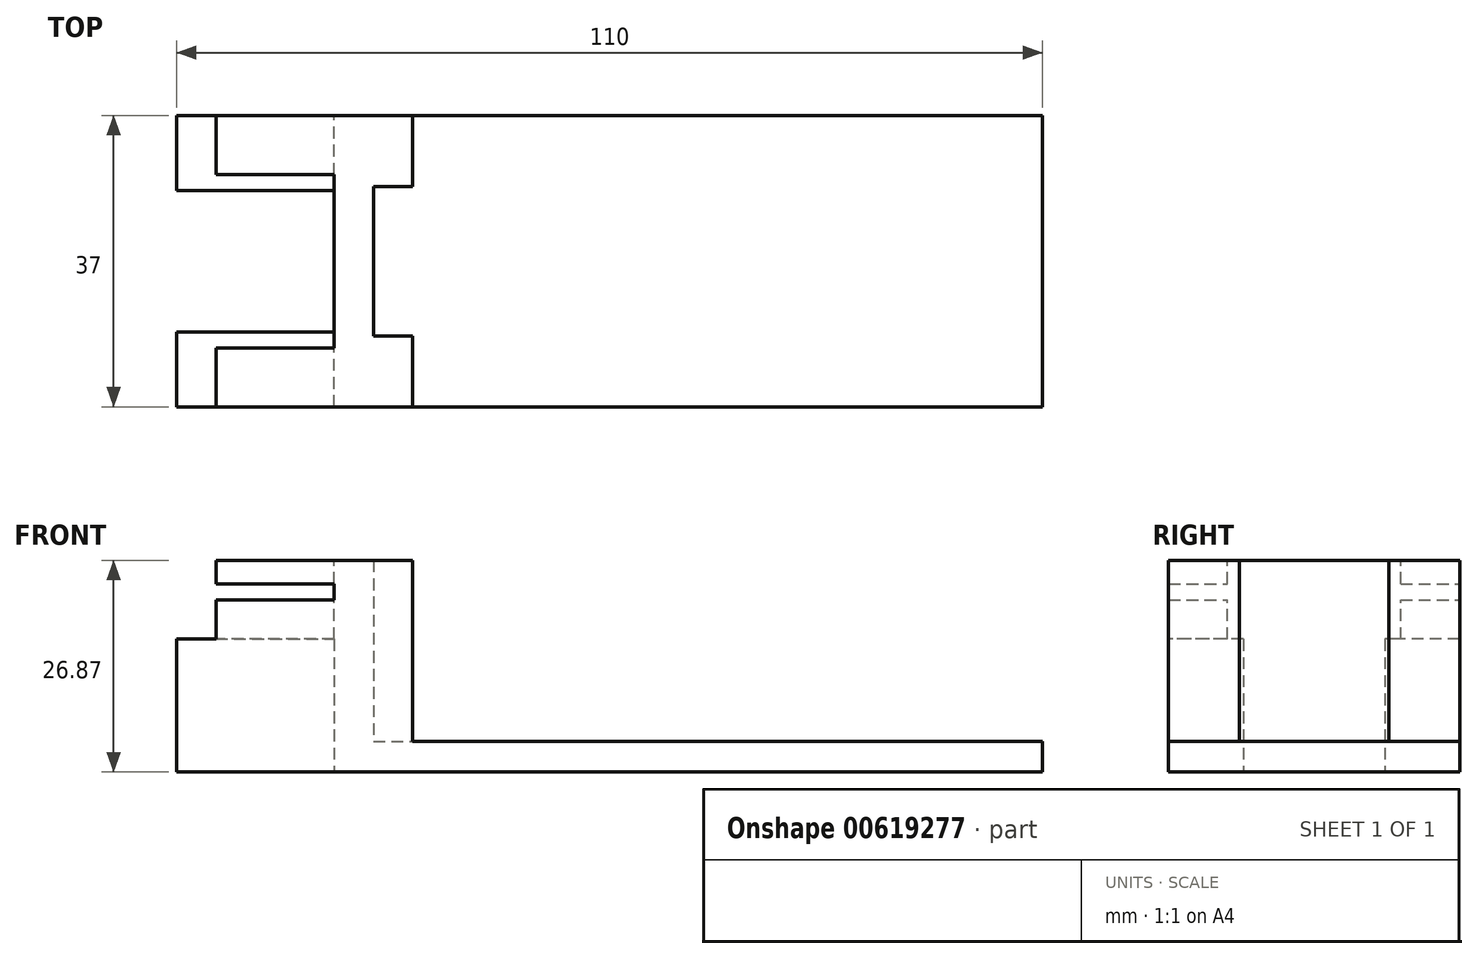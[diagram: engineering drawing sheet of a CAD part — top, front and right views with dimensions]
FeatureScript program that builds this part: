
annotation { "Feature Type Name" : "Feature", "Feature Type Description" : "" }
export const myFeature = defineFeature(function(context is Context, id is Id, definition is map)
    precondition{}
    {
        {
            var Q0;
            Q0=qCreatedBy(makeId("Front.planeOp"),FACE);
            var sketch = newSketch(context, id + "F0", { "sketchPlane" : qUnion([Q0])});
            skLineSegment(sketch, "E0.bottom", {"start": v(-14.48, -27.76) * mm, "end": v(15.52, -27.76) * mm});
            skLineSegment(sketch, "E0.top", {"start": v(-14.48, -54.63) * mm, "end": v(15.52, -54.63) * mm});
            skLineSegment(sketch, "E0.left", {"start": v(-14.48, -27.76) * mm, "end": v(-14.48, -54.63) * mm});
            skLineSegment(sketch, "E0.right", {"start": v(15.52, -27.76) * mm, "end": v(15.52, -50.78) * mm});
            skLineSegment(sketch, "E1.bottom", {"start": v(15.52, -54.63) * mm, "end": v(95.52, -54.63) * mm});
            skLineSegment(sketch, "E1.top", {"start": v(15.52, -50.78) * mm, "end": v(95.52, -50.78) * mm});
            skLineSegment(sketch, "E1.right", {"start": v(95.52, -54.63) * mm, "end": v(95.52, -50.78) * mm});
            skSolve(sketch);
        }
        {
            var Q0;
            Q0 = qSketchRegion(id + "F0", true);
            extrude(context, id + "F1", {"entities" : qUnion([Q0]), "depth" : 37 * mm, "offsetDistance" : 25.4 * mm});
        }
        {
            var Q0;
            Q0=makeQuery(id+"F1.opExtrude","SWEPT_FACE",FACE,{"disambiguationData":[OSD([sQuery(id+"F0.wireOp",EDGE,"E0.right")])]});
            var sketch = newSketch(context, id + "F2", { "sketchPlane" : qUnion([Q0])});
            skLineSegment(sketch, "E2.bottom", {"start": v(-28, -27.76) * mm, "end": v(-9, -27.76) * mm});
            skLineSegment(sketch, "E2.top", {"start": v(-28, -50.78) * mm, "end": v(-9, -50.78) * mm});
            skLineSegment(sketch, "E2.left", {"start": v(-28, -27.76) * mm, "end": v(-28, -50.78) * mm});
            skLineSegment(sketch, "E2.right", {"start": v(-9, -27.76) * mm, "end": v(-9, -50.78) * mm});
            skSolve(sketch);
        }
        {
            var Q0;
            Q0 = qSketchRegion(id + "F2", true);
            extrude(context, id + "F3", {"entities" : qUnion([Q0]), "operationType" : NewBodyOperationType.REMOVE, "oppositeDirection" : true, "depth" : 5 * mm, "offsetDistance" : 25.4 * mm});
        }
        {
            var Q0;
            Q0=makeQuery(id+"F1.opExtrude","SWEPT_FACE",FACE,{"disambiguationData":[OSD([sQuery(id+"F0.wireOp",EDGE,"E0.left")])]});
            var sketch = newSketch(context, id + "F4", { "sketchPlane" : qUnion([Q0])});
            skLineSegment(sketch, "E3.bottom", {"start": v(27.5, -27.76) * mm, "end": v(9.5, -27.76) * mm});
            skLineSegment(sketch, "E3.top", {"start": v(27.5, -54.63) * mm, "end": v(9.5, -54.63) * mm});
            skLineSegment(sketch, "E3.left", {"start": v(27.5, -27.76) * mm, "end": v(27.5, -54.63) * mm});
            skLineSegment(sketch, "E3.right", {"start": v(9.5, -27.76) * mm, "end": v(9.5, -54.63) * mm});
            skSolve(sketch);
        }
        {
            var Q0;
            Q0 = qSketchRegion(id + "F4", true);
            extrude(context, id + "F5", {"entities" : qUnion([Q0]), "operationType" : NewBodyOperationType.REMOVE, "oppositeDirection" : true, "depth" : 20 * mm, "offsetDistance" : 25.4 * mm});
        }
        {
            var Q0;
            {var subQ2=sQuery(id+"F0.wireOp",EDGE,"E0.left");Q0=makeQuery(id+"F5.boolean.opBoolean","SPLIT",FACE,{"disambiguationData":[TD([makeQuery(id+"F5.opExtrude","SWEPT_FACE",FACE,{"disambiguationData":[OSD([sQuery(id+"F4.wireOp",EDGE,"E3.right")])]})])],"derivedFrom":makeQuery(id+"F1.opExtrude","SWEPT_FACE",FACE,{"disambiguationData":[OSD([subQ2])]})});}
            var sketch = newSketch(context, id + "F6", { "sketchPlane" : qUnion([Q0])});
            skLineSegment(sketch, "E4.bottom", {"start": v(0, -30.76) * mm, "end": v(37, -30.76) * mm});
            skLineSegment(sketch, "E4.top", {"start": v(0, -32.76) * mm, "end": v(37, -32.76) * mm});
            skLineSegment(sketch, "E4.left", {"start": v(0, -30.76) * mm, "end": v(0, -32.76) * mm});
            skLineSegment(sketch, "E4.right", {"start": v(37, -30.76) * mm, "end": v(37, -32.76) * mm});
            skSolve(sketch);
        }
        {
            var Q0;
            Q0 = qSketchRegion(id + "F6", true);
            var Q1;
            Q1=makeQuery(id+"F5.boolean.opBoolean","COPY",FACE,{"derivedFrom":makeQuery(id+"F5.opExtrude","CAP_FACE",FACE,{"disambiguationData":[OSD([sQuery(id+"F4.wireOp",EDGE,"E3.bottom"),sQuery(id+"F4.wireOp",EDGE,"E3.top"),sQuery(id+"F4.wireOp",EDGE,"E3.left"),sQuery(id+"F4.wireOp",EDGE,"E3.right")])],"isStart":false})});
            extrude(context, id + "F7", {"entities" : qUnion([Q0]), "operationType" : NewBodyOperationType.REMOVE, "endBound" : BoundingType.UP_TO_SURFACE, "oppositeDirection" : true, "depth" : 25.4 * mm, "endBoundEntityFace" : qUnion([Q1]), "offsetDistance" : 25.4 * mm});
        }
        {
            var Q0;
            {var subQ1=sQuery(id+"F0.wireOp",EDGE,"E0.left");var subQ6=makeQuery(id+"F5.opExtrude","SWEPT_FACE",FACE,{"disambiguationData":[OSD([sQuery(id+"F4.wireOp",EDGE,"E3.right")])]});Q0=makeQuery(id+"F7.boolean.opBoolean","SPLIT",FACE,{"disambiguationData":[TD([makeQuery(id+"F7.opExtrude","SWEPT_FACE",FACE,{"disambiguationData":[OSD([sQuery(id+"F6.wireOp",EDGE,"E4.top")])]})])],"derivedFrom":makeQuery(id+"F5.boolean.opBoolean","SPLIT",FACE,{"disambiguationData":[TD([subQ6])],"derivedFrom":makeQuery(id+"F1.opExtrude","SWEPT_FACE",FACE,{"disambiguationData":[OSD([subQ1])]})})});}
            var sketch = newSketch(context, id + "F8", { "sketchPlane" : qUnion([Q0])});
            skLineSegment(sketch, "E5.bottom", {"start": v(0, -27.76) * mm, "end": v(37, -27.76) * mm});
            skLineSegment(sketch, "E5.top", {"start": v(0, -37.76) * mm, "end": v(37, -37.76) * mm});
            skLineSegment(sketch, "E5.left", {"start": v(0, -27.76) * mm, "end": v(0, -37.76) * mm});
            skLineSegment(sketch, "E5.right", {"start": v(37, -27.76) * mm, "end": v(37, -37.76) * mm});
            skSolve(sketch);
        }
        {
            var Q0;
            Q0 = qSketchRegion(id + "F8", true);
            extrude(context, id + "F9", {"entities" : qUnion([Q0]), "operationType" : NewBodyOperationType.REMOVE, "oppositeDirection" : true, "depth" : 5 * mm, "offsetDistance" : 25.4 * mm});
        }
        {
            var Q0;
            Q0=makeQuery(id+"F1.opExtrude","SWEPT_FACE",FACE,{"disambiguationData":[OSD([sQuery(id+"F0.wireOp",EDGE,"E0.bottom")])]});
            var sketch = newSketch(context, id + "F10", { "sketchPlane" : qUnion([Q0])});
            skLineSegment(sketch, "E6.bottom", {"start": v(-14.48, -7.5) * mm, "end": v(5.52, -7.5) * mm});
            skLineSegment(sketch, "E6.top", {"start": v(-14.48, -29.5) * mm, "end": v(5.52, -29.5) * mm});
            skLineSegment(sketch, "E6.left", {"start": v(-14.48, -7.5) * mm, "end": v(-14.48, -29.5) * mm});
            skLineSegment(sketch, "E6.right", {"start": v(5.52, -7.5) * mm, "end": v(5.52, -29.5) * mm});
            skSolve(sketch);
        }
        {
            var Q0;
            Q0 = qSketchRegion(id + "F10", true);
            var Q1;
            {var subQ1=sQuery(id+"F8.wireOp",EDGE,"E5.top");Q1=makeQuery(id+"F9.boolean.opBoolean","COPY",FACE,{"disambiguationData":[TD([makeQuery(id+"F5.boolean.opBoolean","COPY",FACE,{"derivedFrom":makeQuery(id+"F5.opExtrude","SWEPT_FACE",FACE,{"disambiguationData":[OSD([sQuery(id+"F4.wireOp",EDGE,"E3.right")])]})})])],"derivedFrom":makeQuery(id+"F9.opExtrude","SWEPT_FACE",FACE,{"disambiguationData":[OSD([subQ1])]})});}
            extrude(context, id + "F11", {"entities" : qUnion([Q0]), "operationType" : NewBodyOperationType.REMOVE, "endBound" : BoundingType.UP_TO_SURFACE, "oppositeDirection" : true, "depth" : 7 * mm, "endBoundEntityFace" : qUnion([Q1]), "offsetDistance" : 25.4 * mm});
        }
    });
